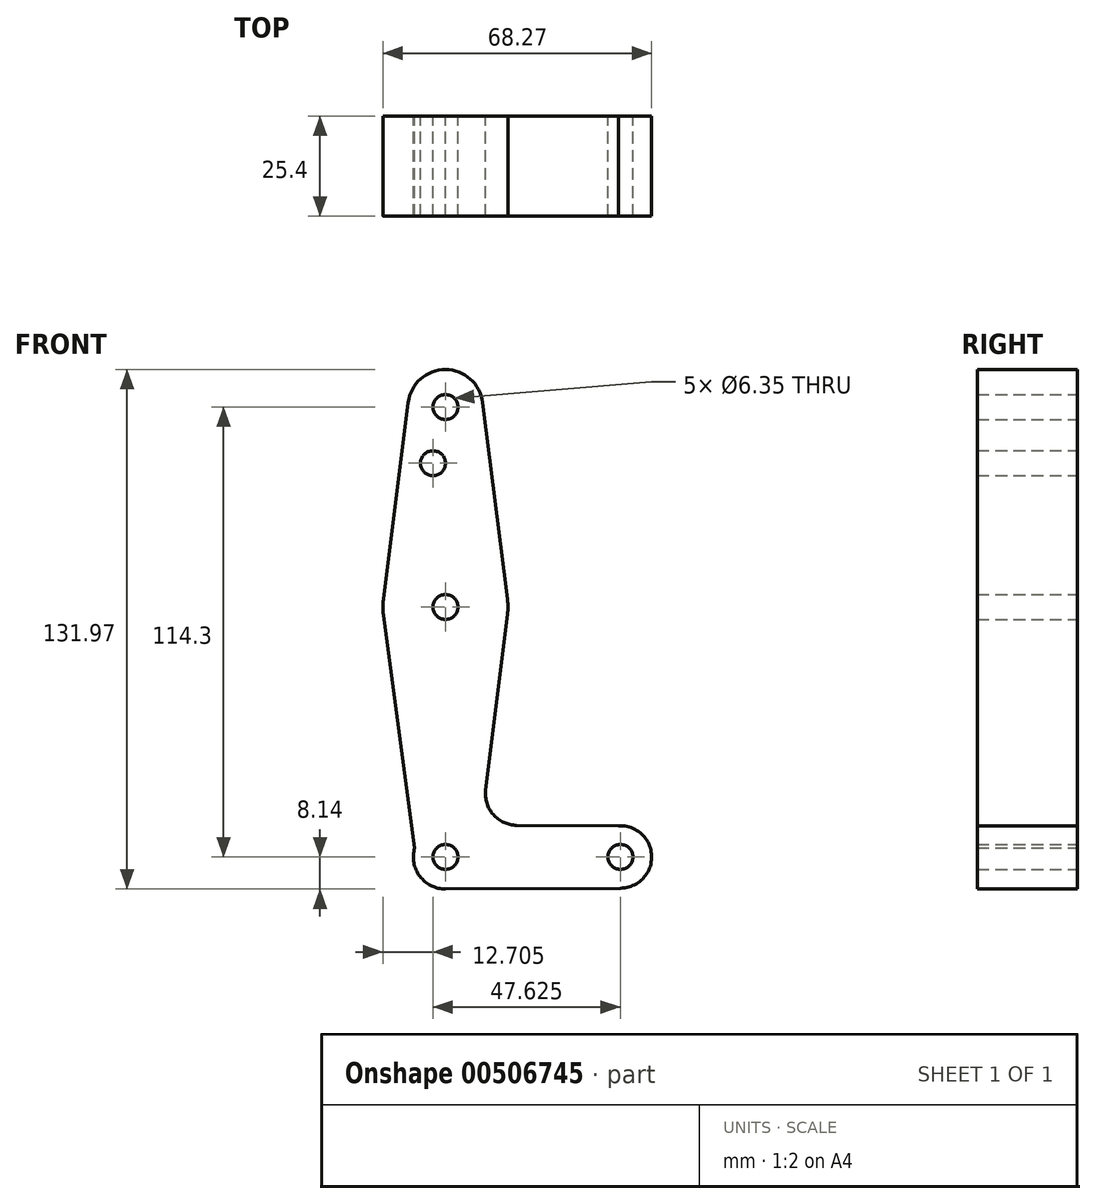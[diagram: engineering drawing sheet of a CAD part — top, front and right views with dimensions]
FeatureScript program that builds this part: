
annotation { "Feature Type Name" : "Feature", "Feature Type Description" : "" }
export const myFeature = defineFeature(function(context is Context, id is Id, definition is map)
    precondition{}
    {
        {
            var Q0;
            Q0=qCreatedBy(makeId("Front.planeOp"),FACE);
            var sketch = newSketch(context, id + "F0", { "sketchPlane" : qUnion([Q0])});
            skLineSegment(sketch, "E0", {"start": v(0, 0) * mm, "end": v(0, 114.3) * mm, "construction": true});
            skLineSegment(sketch, "E1", {"start": v(0, 0) * mm, "end": v(44.45, 0) * mm, "construction": true});
            skCircle(sketch, "E2", {"center": v(0, 114.3) * mm, "radius": 9.52 * mm});
            skCircle(sketch, "E3", {"center": v(0, 0) * mm, "radius": 8.14 * mm});
            skCircle(sketch, "E4", {"center": v(44.45, 0) * mm, "radius": 7.94 * mm});
            skCircle(sketch, "E5", {"center": v(0, 63.5) * mm, "radius": 15.88 * mm});
            skLineSegment(sketch, "E6", {"start": v(-9.45, 115.5) * mm, "end": v(-15.75, 65.48) * mm});
            skLineSegment(sketch, "E7", {"start": v(0, -8.14) * mm, "end": v(44.49, -7.94) * mm});
            skLineSegment(sketch, "E8", {"start": v(9.45, 115.5) * mm, "end": v(15.75, 65.48) * mm});
            skCircle(sketch, "E9", {"center": v(0, 114.3) * mm, "radius": 3.18 * mm});
            skCircle(sketch, "E10", {"center": v(0, 63.5) * mm, "radius": 3.18 * mm});
            skCircle(sketch, "E11", {"center": v(0, 0) * mm, "radius": 3.18 * mm});
            skCircle(sketch, "E12", {"center": v(44.45, 0) * mm, "radius": 3.18 * mm});
            skCircle(sketch, "E13", {"center": v(-3.18, 100.03) * mm, "radius": 3.18 * mm});
            skLineSegment(sketch, "E14", {"start": v(44.02, 7.93) * mm, "end": v(18.1, 8.05) * mm});
            skLineSegment(sketch, "E15", {"start": v(-7.81, 2.3) * mm, "end": v(-15.73, 61.4) * mm});
            skLineSegment(sketch, "E16", {"start": v(10.24, 16.98) * mm, "end": v(15.75, 61.55) * mm});
            skArc(sketch, "E17.filletArc", {"start": v(10.24, 16.98) * mm, "mid": v(12.16, 10.75) * mm, "end": v(18.1, 8.05) * mm});
            skSolve(sketch);
        }
        {
            var Q0;
            Q0 = qSketchRegion(id + "F0", true);
            extrude(context, id + "F1", {"entities" : qUnion([Q0]), "depth" : 25.4 * mm});
        }
        {
            var Q0;
            Q0 = qSketchRegion(id + "F0", true);
            extrude(context, id + "F2", {"entities" : qUnion([Q0]), "operationType" : NewBodyOperationType.ADD, "depth" : 3.05 * mm});
        }
    });
